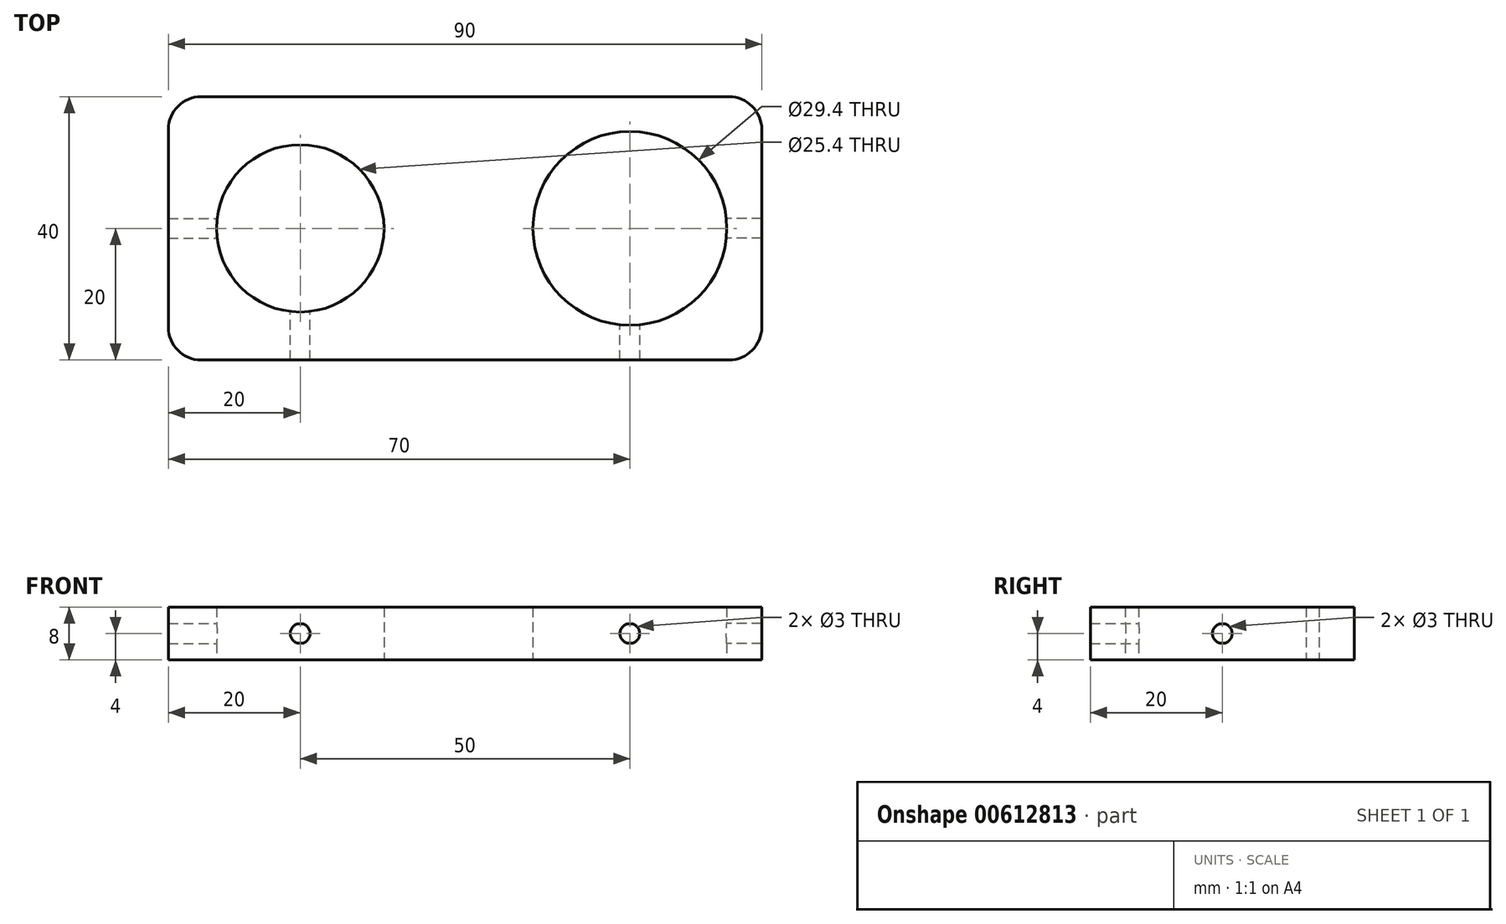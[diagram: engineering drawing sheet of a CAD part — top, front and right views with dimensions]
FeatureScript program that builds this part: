
annotation { "Feature Type Name" : "Feature", "Feature Type Description" : "" }
export const myFeature = defineFeature(function(context is Context, id is Id, definition is map)
    precondition{}
    {
        {
            var Q0;
            Q0=qCreatedBy(makeId("Top.planeOp"),FACE);
            var sketch = newSketch(context, id + "F0", { "sketchPlane" : qUnion([Q0])});
            skCircle(sketch, "E0", {"center": v(0, 0) * mm, "radius": 12.7 * mm});
            skCircle(sketch, "E1", {"center": v(50, 0) * mm, "radius": 14.7 * mm});
            skLineSegment(sketch, "E2", {"start": v(50, 20) * mm, "end": v(0, 20) * mm});
            skLineSegment(sketch, "E3", {"start": v(0, -20) * mm, "end": v(50, -20) * mm});
            skLineSegment(sketch, "E4.bottom", {"start": v(0, 20) * mm, "end": v(-20, 20) * mm});
            skLineSegment(sketch, "E4.top", {"start": v(0, -20) * mm, "end": v(-20, -20) * mm});
            skLineSegment(sketch, "E4.left", {"start": v(0, 20) * mm, "end": v(0, -20) * mm});
            skLineSegment(sketch, "E4.right", {"start": v(-20, 20) * mm, "end": v(-20, -20) * mm});
            skLineSegment(sketch, "E5.bottom", {"start": v(50, 20) * mm, "end": v(70, 20) * mm});
            skLineSegment(sketch, "E5.top", {"start": v(50, -20) * mm, "end": v(70, -20) * mm});
            skLineSegment(sketch, "E5.left", {"start": v(50, 20) * mm, "end": v(50, -20) * mm});
            skLineSegment(sketch, "E5.right", {"start": v(70, 20) * mm, "end": v(70, -20) * mm});
            skSolve(sketch);
        }
        {
            var Q0;
            {var subQ0=sQuery(id+"F0.wireOp",EDGE,"E2");Q0=makeQuery(id+"F0.imprint","IMPRINT",FACE,{"disambiguationData":[TD([[makeQuery(id+"F0.imprint","IMPRINT",EDGE,{"derivedFrom":subQ0}),1.0]])]});}
            var Q1;
            Q1=makeQuery(id+"F0.imprint","IMPRINT",FACE,{"disambiguationData":[TD([[makeQuery(id+"F0.imprint","IMPRINT",EDGE,{"derivedFrom":sQuery(id+"F0.wireOp",EDGE,"E0")}),-1.0]])]});
            var Q2;
            Q2=makeQuery(id+"F0.imprint","IMPRINT",FACE,{"disambiguationData":[TD([[makeQuery(id+"F0.imprint","IMPRINT",EDGE,{"derivedFrom":sQuery(id+"F0.wireOp",EDGE,"E1")}),-1.0]])]});
            extrude(context, id + "F1", {"entities" : qUnion([Q0, Q1, Q2]), "depth" : 8 * mm, "offsetDistance" : 25 * mm});
        }
        {
            var Q0;
            Q0=qCreatedBy(makeId("Front.planeOp"),FACE);
            var sketch = newSketch(context, id + "F2", { "sketchPlane" : qUnion([Q0])});
            skCircle(sketch, "E6", {"center": v(0, 4) * mm, "radius": 1.5 * mm});
            skCircle(sketch, "E7", {"center": v(50, 4) * mm, "radius": 1.5 * mm});
            skSolve(sketch);
        }
        {
            var Q0;
            Q0=makeQuery(id+"F2.imprint","IMPRINT",FACE,{"disambiguationData":[TD([[makeQuery(id+"F2.imprint","IMPRINT",EDGE,{"derivedFrom":sQuery(id+"F2.wireOp",EDGE,"E6")}),1.0]])]});
            var Q1;
            Q1=makeQuery(id+"F2.imprint","IMPRINT",FACE,{"disambiguationData":[TD([[makeQuery(id+"F2.imprint","IMPRINT",EDGE,{"derivedFrom":sQuery(id+"F2.wireOp",EDGE,"E7")}),1.0]])]});
            extrude(context, id + "F3", {"entities" : qUnion([Q0, Q1]), "operationType" : NewBodyOperationType.REMOVE, "depth" : 25 * mm, "offsetDistance" : 25 * mm});
        }
        {
            var Q0;
            Q0=qCreatedBy(makeId("Right.planeOp"),FACE);
            var sketch = newSketch(context, id + "F4", { "sketchPlane" : qUnion([Q0])});
            skCircle(sketch, "E8", {"center": v(0, 4) * mm, "radius": 1.5 * mm});
            skSolve(sketch);
        }
        {
            var Q0;
            Q0=makeQuery(id+"F4.imprint","IMPRINT",FACE,{"disambiguationData":[TD([[makeQuery(id+"F4.imprint","IMPRINT",EDGE,{"derivedFrom":sQuery(id+"F4.wireOp",EDGE,"E8")}),1.0]])]});
            extrude(context, id + "F5", {"entities" : qUnion([Q0]), "operationType" : NewBodyOperationType.REMOVE, "oppositeDirection" : true, "depth" : 25 * mm, "offsetDistance" : 25 * mm});
        }
        {
            var Q0;
            Q0=makeQuery(id+"F4.imprint","IMPRINT",FACE,{"disambiguationData":[TD([[makeQuery(id+"F4.imprint","IMPRINT",EDGE,{"derivedFrom":sQuery(id+"F4.wireOp",EDGE,"E8")}),1.0]])]});
            extrude(context, id + "F6", {"entities" : qUnion([Q0]), "operationType" : NewBodyOperationType.REMOVE, "depth" : 82.2 * mm, "offsetDistance" : 25 * mm, "hasSecondDirection" : true, "secondDirectionOppositeDirection" : false, "secondDirectionDepth" : 54.3 * mm});
        }
        {
            var Q0;
            Q0=makeQuery(id+"F1.opExtrude","SWEPT_EDGE",EDGE,{"disambiguationData":[OSD([sQuery(id+"F0.wireOp",EDGE,"E5.bottom"),sQuery(id+"F0.wireOp",EDGE,"E5.right")])]});
            var Q1;
            Q1=makeQuery(id+"F1.opExtrude","SWEPT_EDGE",EDGE,{"disambiguationData":[OSD([sQuery(id+"F0.wireOp",EDGE,"E5.top"),sQuery(id+"F0.wireOp",EDGE,"E5.right")])]});
            var Q2;
            Q2=makeQuery(id+"F1.opExtrude","SWEPT_EDGE",EDGE,{"disambiguationData":[OSD([sQuery(id+"F0.wireOp",EDGE,"E4.bottom"),sQuery(id+"F0.wireOp",EDGE,"E4.right")])]});
            var Q3;
            Q3=makeQuery(id+"F1.opExtrude","SWEPT_EDGE",EDGE,{"disambiguationData":[OSD([sQuery(id+"F0.wireOp",EDGE,"E4.top"),sQuery(id+"F0.wireOp",EDGE,"E4.right")])]});
            fillet(context, id + "F7", {"entities" : qUnion([Q0, Q1, Q2, Q3]), "radius" : 5 * mm, "tangentPropagation" : true, "allowEdgeOverflow" : false});
        }
    });
